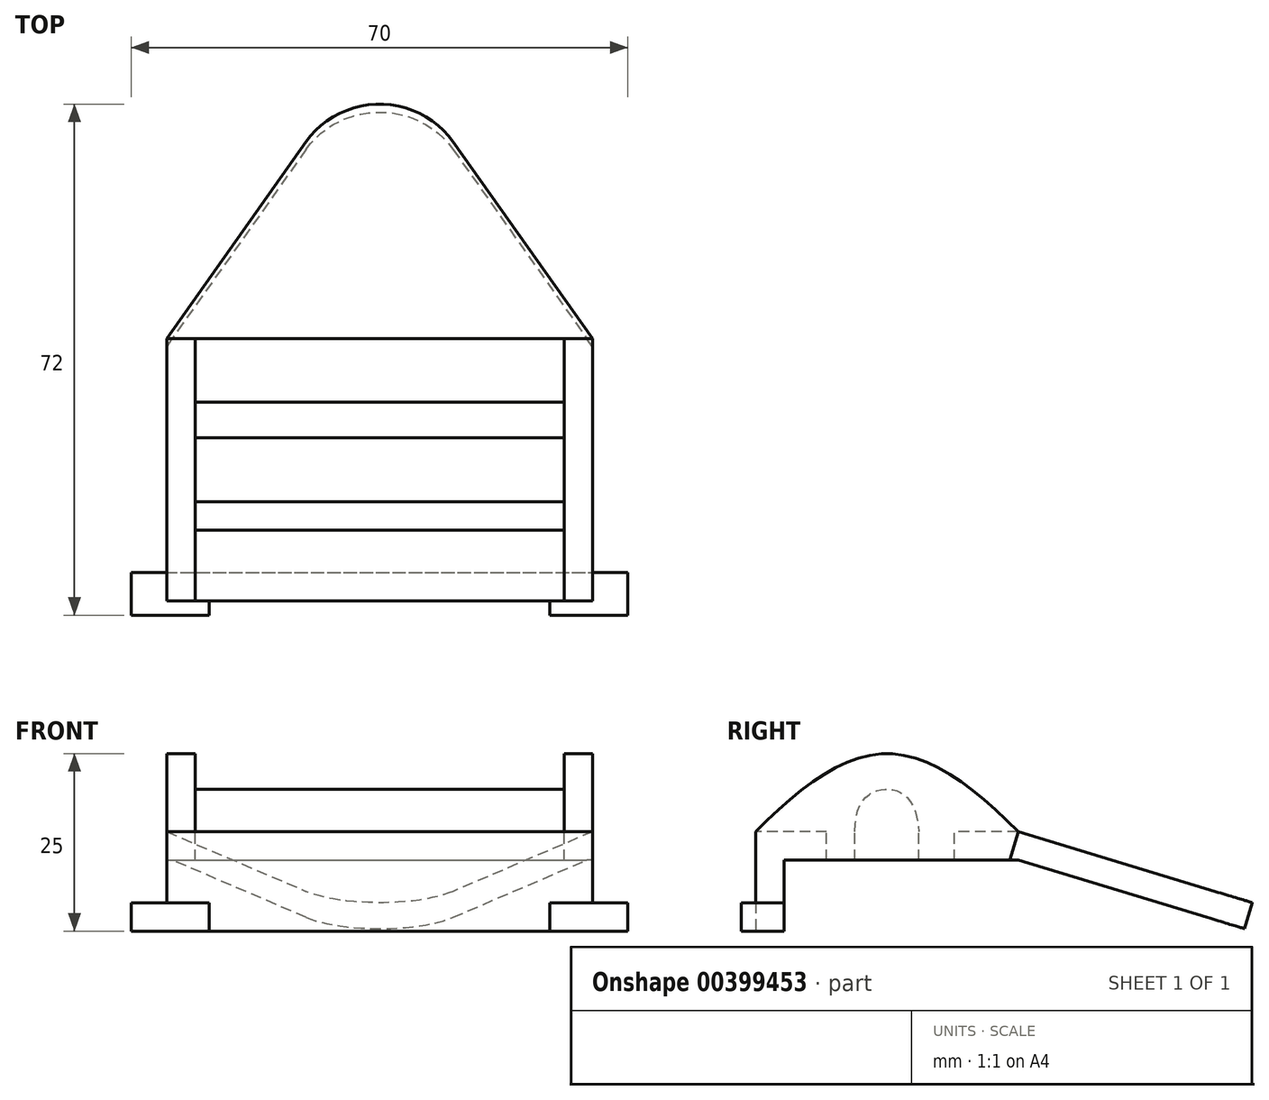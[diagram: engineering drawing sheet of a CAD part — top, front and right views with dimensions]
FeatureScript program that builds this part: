
annotation { "Feature Type Name" : "Feature", "Feature Type Description" : "" }
export const myFeature = defineFeature(function(context is Context, id is Id, definition is map)
    precondition{}
    {
        {
            var Q0;
            Q0=qCreatedBy(makeId("Top.planeOp"),FACE);
            var sketch = newSketch(context, id + "F0", { "sketchPlane" : qUnion([Q0])});
            skLineSegment(sketch, "E0.bottom", {"start": v(-30, 18.5) * mm, "end": v(30, 18.5) * mm});
            skLineSegment(sketch, "E0.top", {"start": v(-30, -18.5) * mm, "end": v(30, -18.5) * mm});
            skLineSegment(sketch, "E0.left", {"start": v(-30, 18.5) * mm, "end": v(-30, -18.5) * mm});
            skLineSegment(sketch, "E0.right", {"start": v(30, 18.5) * mm, "end": v(30, -18.5) * mm});
            skSolve(sketch);
        }
        {
            var Q0;
            Q0 = qSketchRegion(id + "F0", true);
            extrude(context, id + "F1", {"entities" : qUnion([Q0]), "oppositeDirection" : true, "depth" : 4 * mm});
        }
        {
            var Q0;
            Q0=makeQuery(id+"F1.opExtrude","SWEPT_FACE",FACE,{"disambiguationData":[OSD([sQuery(id+"F0.wireOp",EDGE,"E0.right")])]});
            var sketch = newSketch(context, id + "F2", { "sketchPlane" : qUnion([Q0])});
            skFitSpline(sketch, "E1", {"points": [v(-18.5, 0) * mm, v(0, 11) * mm, v(18.5, 0) * mm], "startDerivative": vector(37, 37.5) * mm, "endDerivative": vector(37, -37.5) * mm});
            skLineSegment(sketch, "E2", {"start": v(-18.5, 0) * mm, "end": v(18.5, 0) * mm});
            skSolve(sketch);
        }
        {
            var Q0;
            Q0=makeQuery(id+"F2.imprint","IMPRINT",FACE,{"disambiguationData":[TD([[makeQuery(id+"F2.imprint","IMPRINT",EDGE,{"derivedFrom":sQuery(id+"F2.wireOp",EDGE,"E1")}),-1.0]])]});
            extrude(context, id + "F3", {"entities" : qUnion([Q0]), "oppositeDirection" : true, "depth" : 4 * mm});
        }
        {
            var Q0;
            Q0=makeQuery(id+"F3.opExtrude","SWEPT_BODY",BODY,{"disambiguationData":[OSD([sQuery(id+"F2.wireOp",EDGE,"E1"),sQuery(id+"F2.wireOp",EDGE,"E2")])]});
            var Q1;
            Q1=qCreatedBy(makeId("Right.planeOp"),FACE);
            mirror(context, id + "F4", {"operationType" : NewBodyOperationType.ADD, "entities" : qUnion([Q0]), "mirrorPlane" : qUnion([Q1])});
        }
        {
            var Q0;
            Q0=makeQuery(id+"F4.boolean.opBoolean","MERGE",FACE,{"derivedFrom":[makeQuery(id+"F1.opExtrude","SWEPT_FACE",FACE,{"disambiguationData":[OSD([sQuery(id+"F0.wireOp",EDGE,"E0.right")])]}),makeQuery(id+"F3.opExtrude","CAP_FACE",FACE,{"disambiguationData":[OSD([sQuery(id+"F2.wireOp",EDGE,"E1"),sQuery(id+"F2.wireOp",EDGE,"E2")])],"isStart":true})]});
            var sketch = newSketch(context, id + "F5", { "sketchPlane" : qUnion([Q0])});
            skFitSpline(sketch, "E3", {"points": [v(-4.5, 0) * mm, v(0, 6) * mm, v(4.5, 0) * mm], "startDerivative": vector(-0.64, 27) * mm, "endDerivative": vector(1.63, -27) * mm});
            skLineSegment(sketch, "E4", {"start": v(-4.5, 0) * mm, "end": v(4.5, 0) * mm});
            skSolve(sketch);
        }
        {
            var Q0;
            Q0 = qSketchRegion(id + "F5", true);
            var Q1;
            Q1=makeQuery(id+"F4.boolean.opBoolean","MERGE",FACE,{"derivedFrom":[makeQuery(id+"F1.opExtrude","SWEPT_FACE",FACE,{"disambiguationData":[OSD([sQuery(id+"F0.wireOp",EDGE,"E0.left")])]}),makeQuery(id+"F4.opPattern","COPY",FACE,{"derivedFrom":makeQuery(id+"F3.opExtrude","CAP_FACE",FACE,{"disambiguationData":[OSD([sQuery(id+"F2.wireOp",EDGE,"E1"),sQuery(id+"F2.wireOp",EDGE,"E2")])],"isStart":true}),"instanceName":"1"})]});
            extrude(context, id + "F6", {"entities" : qUnion([Q0]), "operationType" : NewBodyOperationType.ADD, "endBound" : BoundingType.UP_TO_SURFACE, "oppositeDirection" : true, "endBoundEntityFace" : qUnion([Q1]), "depth" : 25 * mm});
        }
        {
            var Q0;
            {var subQ3=sQuery(id+"F0.wireOp",EDGE,"E0.top");Q0=makeQuery(id+"F6.boolean.opBoolean","SPLIT",FACE,{"disambiguationData":[TD([makeQuery(id+"F1.opExtrude","SWEPT_FACE",FACE,{"disambiguationData":[OSD([subQ3])]})])],"derivedFrom":makeQuery(id+"F1.opExtrude","CAP_FACE",FACE,{"disambiguationData":[OSD([sQuery(id+"F0.wireOp",EDGE,"E0.bottom"),subQ3,sQuery(id+"F0.wireOp",EDGE,"E0.left"),sQuery(id+"F0.wireOp",EDGE,"E0.right")])],"isStart":true})});}
            var sketch = newSketch(context, id + "F7", { "sketchPlane" : qUnion([Q0])});
            skLineSegment(sketch, "E5.bottom", {"start": v(-26, -4.5) * mm, "end": v(26, -4.5) * mm});
            skLineSegment(sketch, "E5.top", {"start": v(-26, -8.5) * mm, "end": v(26, -8.5) * mm});
            skLineSegment(sketch, "E5.left", {"start": v(-26, -4.5) * mm, "end": v(-26, -8.5) * mm});
            skLineSegment(sketch, "E5.right", {"start": v(26, -4.5) * mm, "end": v(26, -8.5) * mm});
            skSolve(sketch);
        }
        {
            var Q0;
            {var subQ3=sQuery(id+"F0.wireOp",EDGE,"E0.bottom");Q0=makeQuery(id+"F6.boolean.opBoolean","SPLIT",FACE,{"disambiguationData":[TD([makeQuery(id+"F1.opExtrude","SWEPT_FACE",FACE,{"disambiguationData":[OSD([subQ3])]})])],"derivedFrom":makeQuery(id+"F1.opExtrude","CAP_FACE",FACE,{"disambiguationData":[OSD([subQ3,sQuery(id+"F0.wireOp",EDGE,"E0.top"),sQuery(id+"F0.wireOp",EDGE,"E0.left"),sQuery(id+"F0.wireOp",EDGE,"E0.right")])],"isStart":true})});}
            var sketch = newSketch(context, id + "F8", { "sketchPlane" : qUnion([Q0])});
            skLineSegment(sketch, "E6.bottom", {"start": v(-26, 4.5) * mm, "end": v(26, 4.5) * mm});
            skLineSegment(sketch, "E6.top", {"start": v(-26, 9.5) * mm, "end": v(26, 9.5) * mm});
            skLineSegment(sketch, "E6.left", {"start": v(-26, 4.5) * mm, "end": v(-26, 9.5) * mm});
            skLineSegment(sketch, "E6.right", {"start": v(26, 4.5) * mm, "end": v(26, 9.5) * mm});
            skSolve(sketch);
        }
        {
            var Q0;
            Q0=makeQuery(id+"F8.imprint","IMPRINT",FACE,{"disambiguationData":[TD([[makeQuery(id+"F8.imprint","IMPRINT",EDGE,{"derivedFrom":sQuery(id+"F8.wireOp",EDGE,"E6.bottom")}),1.0]])]});
            var Q1;
            Q1=makeQuery(id+"F7.imprint","IMPRINT",FACE,{"disambiguationData":[TD([[makeQuery(id+"F7.imprint","IMPRINT",EDGE,{"derivedFrom":sQuery(id+"F7.wireOp",EDGE,"E5.bottom")}),-1.0]])]});
            extrude(context, id + "F9", {"entities" : qUnion([Q0, Q1]), "operationType" : NewBodyOperationType.REMOVE, "oppositeDirection" : true, "depth" : 25 * mm});
        }
        {
            var Q0;
            Q0=makeQuery(id+"F1.opExtrude","CAP_FACE",FACE,{"disambiguationData":[OSD([sQuery(id+"F0.wireOp",EDGE,"E0.bottom"),sQuery(id+"F0.wireOp",EDGE,"E0.top"),sQuery(id+"F0.wireOp",EDGE,"E0.left"),sQuery(id+"F0.wireOp",EDGE,"E0.right")])],"isStart":false});
            var sketch = newSketch(context, id + "F10", { "sketchPlane" : qUnion([Q0])});
            skLineSegment(sketch, "E7.bottom", {"start": v(-30, 18.5) * mm, "end": v(30, 18.5) * mm});
            skLineSegment(sketch, "E7.top", {"start": v(-30, 14.5) * mm, "end": v(30, 14.5) * mm});
            skLineSegment(sketch, "E7.left", {"start": v(-30, 18.5) * mm, "end": v(-30, 14.5) * mm});
            skLineSegment(sketch, "E7.right", {"start": v(30, 18.5) * mm, "end": v(30, 14.5) * mm});
            skSolve(sketch);
        }
        {
            var Q0;
            Q0=makeQuery(id+"F10.imprint","IMPRINT",FACE,{"disambiguationData":[TD([[makeQuery(id+"F10.imprint","IMPRINT",EDGE,{"derivedFrom":sQuery(id+"F10.wireOp",EDGE,"E7.bottom")}),-1.0]])]});
            extrude(context, id + "F11", {"entities" : qUnion([Q0]), "operationType" : NewBodyOperationType.ADD, "depth" : 10 * mm});
        }
        {
            var Q0;
            Q0=makeQuery(id+"F11.opExtrude","CAP_FACE",FACE,{"disambiguationData":[OSD([sQuery(id+"F10.wireOp",EDGE,"E7.bottom"),sQuery(id+"F10.wireOp",EDGE,"E7.top"),sQuery(id+"F10.wireOp",EDGE,"E7.left"),sQuery(id+"F10.wireOp",EDGE,"E7.right")])],"isStart":false});
            var sketch = newSketch(context, id + "F12", { "sketchPlane" : qUnion([Q0])});
            skLineSegment(sketch, "E8.bottom", {"start": v(24, 20.5) * mm, "end": v(35, 20.5) * mm});
            skLineSegment(sketch, "E8.top", {"start": v(24, 14.5) * mm, "end": v(35, 14.5) * mm});
            skLineSegment(sketch, "E8.left", {"start": v(24, 20.5) * mm, "end": v(24, 14.5) * mm});
            skLineSegment(sketch, "E8.right", {"start": v(35, 20.5) * mm, "end": v(35, 14.5) * mm});
            skLineSegment(sketch, "E9.bottom", {"start": v(-24, 20.5) * mm, "end": v(-35, 20.5) * mm});
            skLineSegment(sketch, "E9.top", {"start": v(-24, 14.5) * mm, "end": v(-35, 14.5) * mm});
            skLineSegment(sketch, "E9.left", {"start": v(-24, 20.5) * mm, "end": v(-24, 14.5) * mm});
            skLineSegment(sketch, "E9.right", {"start": v(-35, 20.5) * mm, "end": v(-35, 14.5) * mm});
            skSolve(sketch);
        }
        {
            var Q0;
            Q0 = qSketchRegion(id + "F12", true);
            extrude(context, id + "F13", {"entities" : qUnion([Q0]), "operationType" : NewBodyOperationType.ADD, "oppositeDirection" : true, "depth" : 4 * mm});
        }
        {
            var Q0;
            Q0=makeQuery(id+"F11.boolean.opBoolean","MERGE",FACE,{"derivedFrom":[makeQuery(id+"F4.boolean.opBoolean","MERGE",FACE,{"derivedFrom":[makeQuery(id+"F1.opExtrude","SWEPT_FACE",FACE,{"disambiguationData":[OSD([sQuery(id+"F0.wireOp",EDGE,"E0.right")])]}),makeQuery(id+"F3.opExtrude","CAP_FACE",FACE,{"disambiguationData":[OSD([sQuery(id+"F2.wireOp",EDGE,"E1"),sQuery(id+"F2.wireOp",EDGE,"E2")])],"isStart":true})]}),makeQuery(id+"F11.opExtrude","SWEPT_FACE",FACE,{"disambiguationData":[OSD([sQuery(id+"F10.wireOp",EDGE,"E7.right")])]})]});
            var sketch = newSketch(context, id + "F14", { "sketchPlane" : qUnion([Q0])});
            skLineSegment(sketch, "E10", {"start": v(18.5, -4) * mm, "end": v(51.5, -14) * mm});
            skLineSegment(sketch, "E11", {"start": v(51.5, -14) * mm, "end": v(51.5, -10) * mm});
            skLineSegment(sketch, "E12", {"start": v(51.5, -10) * mm, "end": v(18.5, 0) * mm});
            skSolve(sketch);
        }
        {
            var Q0;
            Q0=makeQuery(id+"F14.imprint","IMPRINT",FACE,{"disambiguationData":[TD([[makeQuery(id+"F14.imprint","IMPRINT",EDGE,{"derivedFrom":sQuery(id+"F14.wireOp",EDGE,"E10")}),1.0]])]});
            var Q1;
            Q1=makeQuery(id+"F11.boolean.opBoolean","MERGE",FACE,{"derivedFrom":[makeQuery(id+"F4.boolean.opBoolean","MERGE",FACE,{"derivedFrom":[makeQuery(id+"F1.opExtrude","SWEPT_FACE",FACE,{"disambiguationData":[OSD([sQuery(id+"F0.wireOp",EDGE,"E0.left")])]}),makeQuery(id+"F4.opPattern","COPY",FACE,{"derivedFrom":makeQuery(id+"F3.opExtrude","CAP_FACE",FACE,{"disambiguationData":[OSD([sQuery(id+"F2.wireOp",EDGE,"E1"),sQuery(id+"F2.wireOp",EDGE,"E2")])],"isStart":true}),"instanceName":"1"})]}),makeQuery(id+"F11.opExtrude","SWEPT_FACE",FACE,{"disambiguationData":[OSD([sQuery(id+"F10.wireOp",EDGE,"E7.left")])]})]});
            extrude(context, id + "F15", {"entities" : qUnion([Q0]), "operationType" : NewBodyOperationType.ADD, "endBound" : BoundingType.UP_TO_SURFACE, "oppositeDirection" : true, "endBoundEntityFace" : qUnion([Q1]), "depth" : 25 * mm});
        }
        {
            var Q0;
            Q0=makeQuery(id+"F15.opExtrude","SWEPT_FACE",FACE,{"disambiguationData":[OSD([sQuery(id+"F14.wireOp",EDGE,"E12")])]});
            var sketch = newSketch(context, id + "F16", { "sketchPlane" : qUnion([Q0])});
            skArc(sketch, "E13", {"start": v(10.35, 46.7) * mm, "mid": v(0, 52.19) * mm, "end": v(-10.35, 46.7) * mm});
            skLineSegment(sketch, "E14", {"start": v(-30, 17.7) * mm, "end": v(-10.35, 46.7) * mm});
            skLineSegment(sketch, "E15", {"start": v(30, 17.7) * mm, "end": v(10.35, 46.7) * mm});
            skLineSegment(sketch, "E16", {"start": v(-30, 17.7) * mm, "end": v(-30, 52.19) * mm});
            skLineSegment(sketch, "E17", {"start": v(30, 52.19) * mm, "end": v(30, 17.7) * mm});
            skLineSegment(sketch, "E18", {"start": v(-30, 52.19) * mm, "end": v(-30, 58.48) * mm});
            skLineSegment(sketch, "E19", {"start": v(-30, 58.48) * mm, "end": v(30, 58.48) * mm});
            skLineSegment(sketch, "E20", {"start": v(30, 58.48) * mm, "end": v(30, 52.19) * mm});
            skSolve(sketch);
        }
        {
            var Q0;
            Q0 = qSketchRegion(id + "F16", true);
            extrude(context, id + "F17", {"entities" : qUnion([Q0]), "operationType" : NewBodyOperationType.REMOVE, "oppositeDirection" : true, "depth" : 25 * mm});
        }
    });
